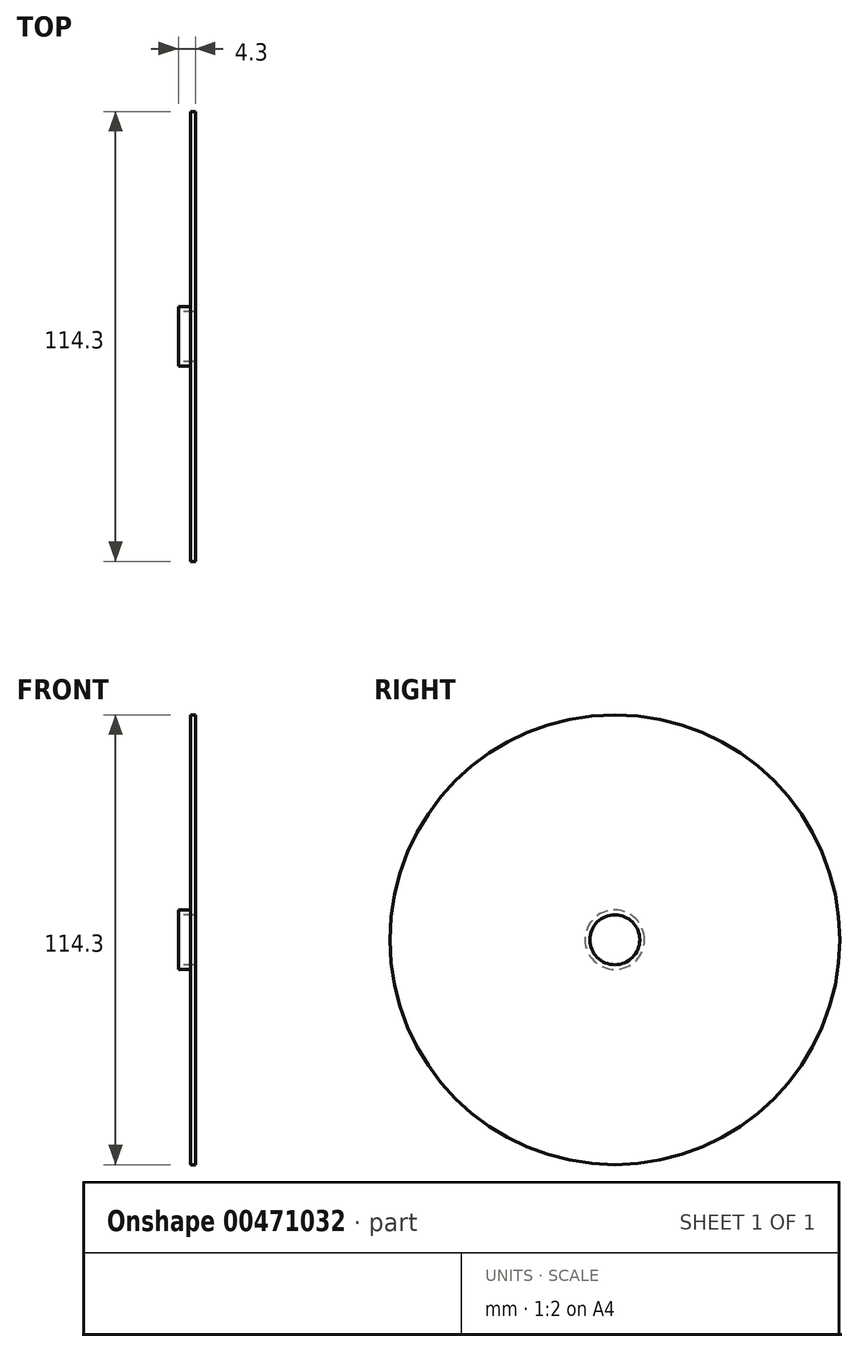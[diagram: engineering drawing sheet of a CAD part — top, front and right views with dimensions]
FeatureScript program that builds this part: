
annotation { "Feature Type Name" : "Feature", "Feature Type Description" : "" }
export const myFeature = defineFeature(function(context is Context, id is Id, definition is map)
    precondition{}
    {
        {
            var Q0;
            Q0=qCreatedBy(makeId("Top.planeOp"),FACE);
            var sketch = newSketch(context, id + "F0", { "sketchPlane" : qUnion([Q0])});
            skLineSegment(sketch, "E0", {"start": v(0, 7.55) * mm, "end": v(3.1, 7.55) * mm});
            skLineSegment(sketch, "E1", {"start": v(3.1, 7.55) * mm, "end": v(3.1, 57.15) * mm});
            skLineSegment(sketch, "E2", {"start": v(3.1, 57.15) * mm, "end": v(4.3, 57.15) * mm});
            skLineSegment(sketch, "E3", {"start": v(4.3, 57.15) * mm, "end": v(4.3, 6.35) * mm});
            skLineSegment(sketch, "E4", {"start": v(4.3, 6.35) * mm, "end": v(0, 6.35) * mm});
            skLineSegment(sketch, "E5", {"start": v(0, 6.35) * mm, "end": v(0, 7.55) * mm});
            skLineSegment(sketch, "E6", {"start": v(0, 0) * mm, "end": v(40.63, 0) * mm, "construction": true});
            skSolve(sketch);
        }
        {
            var Q0;
            Q0=makeQuery(id+"F0.imprint","IMPRINT",FACE,{"disambiguationData":[TD([[makeQuery(id+"F0.imprint","IMPRINT",EDGE,{"derivedFrom":sQuery(id+"F0.wireOp",EDGE,"E0")}),-1.0]])]});
            var Q1;
            Q1=sQuery(id+"F0.wireOp",EDGE,"E6");
            revolve(context, id + "F1", {"entities" : qUnion([Q0]), "axis" : qUnion([Q1]), "revolveType" : RevolveType.FULL});
        }
    });
